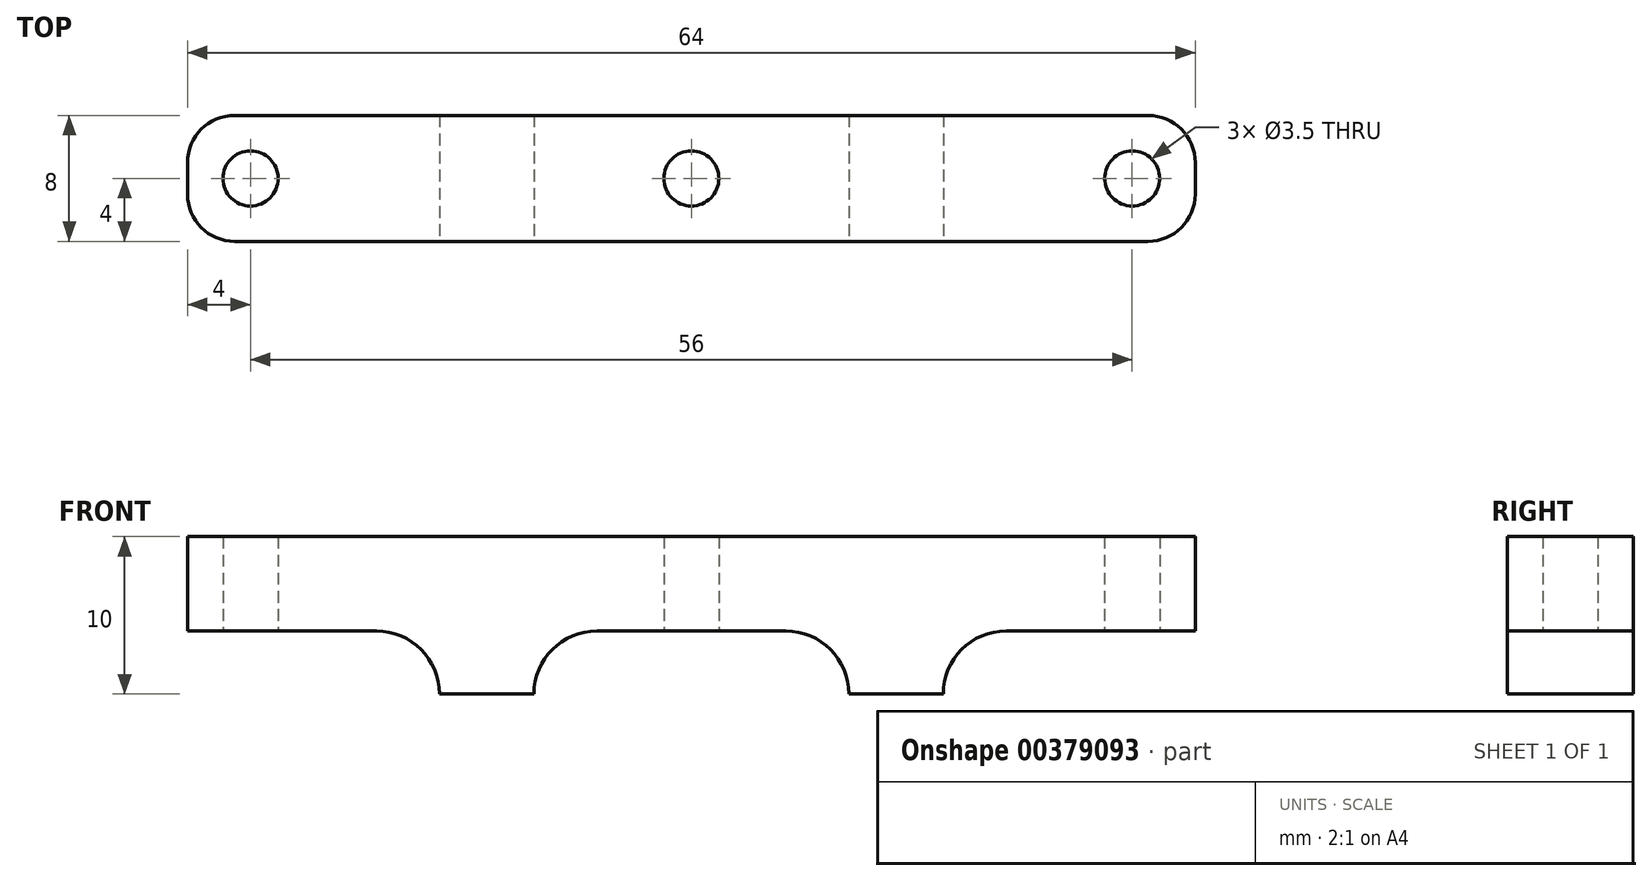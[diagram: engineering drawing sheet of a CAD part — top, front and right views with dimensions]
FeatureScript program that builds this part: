
annotation { "Feature Type Name" : "Feature", "Feature Type Description" : "" }
export const myFeature = defineFeature(function(context is Context, id is Id, definition is map)
    precondition{}
    {
        {
            var Q0;
            Q0=qCreatedBy(makeId("Top.planeOp"),FACE);
            var sketch = newSketch(context, id + "F0", { "sketchPlane" : qUnion([Q0])});
            skLineSegment(sketch, "E0.bottom", {"start": v(0, 0) * mm, "end": v(64, 0) * mm});
            skLineSegment(sketch, "E0.top", {"start": v(0, 8) * mm, "end": v(64, 8) * mm});
            skLineSegment(sketch, "E0.left", {"start": v(0, 0) * mm, "end": v(0, 8) * mm});
            skLineSegment(sketch, "E0.right", {"start": v(64, 0) * mm, "end": v(64, 8) * mm});
            skLineSegment(sketch, "E1", {"start": v(0, 4) * mm, "end": v(64, 4) * mm, "construction": true});
            skCircle(sketch, "E2", {"center": v(4, 4) * mm, "radius": 1.75 * mm});
            skCircle(sketch, "E3", {"center": v(32, 4) * mm, "radius": 1.75 * mm});
            skCircle(sketch, "E4", {"center": v(60, 4) * mm, "radius": 1.75 * mm});
            skSolve(sketch);
        }
        {
            var Q0;
            Q0=makeQuery(id+"F0.imprint","IMPRINT",FACE,{"disambiguationData":[TD([[makeQuery(id+"F0.imprint","IMPRINT",EDGE,{"derivedFrom":sQuery(id+"F0.wireOp",EDGE,"E0.bottom")}),1.0]])]});
            extrude(context, id + "F1", {"entities" : qUnion([Q0]), "depth" : 10 * mm});
        }
        {
            var Q0;
            Q0=makeQuery(id+"F1.opExtrude","SWEPT_FACE",FACE,{"disambiguationData":[OSD([sQuery(id+"F0.wireOp",EDGE,"E0.bottom")])]});
            var sketch = newSketch(context, id + "F2", { "sketchPlane" : qUnion([Q0])});
            skLineSegment(sketch, "E5", {"start": v(0, 4) * mm, "end": v(64, 4) * mm, "construction": true});
            skArc(sketch, "E6", {"start": v(12, 4) * mm, "mid": v(14.83, 2.83) * mm, "end": v(16, 0) * mm});
            skLineSegment(sketch, "E7", {"start": v(16, 0) * mm, "end": v(22, 0) * mm});
            skLineSegment(sketch, "E8", {"start": v(19, 0) * mm, "end": v(19, 4) * mm, "construction": true});
            skArc(sketch, "E9", {"start": v(26, 4) * mm, "mid": v(23.17, 2.83) * mm, "end": v(22, 0) * mm});
            skLineSegment(sketch, "E10", {"start": v(42, 0) * mm, "end": v(48, 0) * mm});
            skLineSegment(sketch, "E11", {"start": v(45, 0) * mm, "end": v(45, 4) * mm, "construction": true});
            skArc(sketch, "E12", {"start": v(38, 4) * mm, "mid": v(40.83, 2.83) * mm, "end": v(42, 0) * mm});
            skArc(sketch, "E13", {"start": v(52, 4) * mm, "mid": v(49.17, 2.83) * mm, "end": v(48, 0) * mm});
            skLineSegment(sketch, "E14", {"start": v(38, 4) * mm, "end": v(26, 4) * mm});
            skLineSegment(sketch, "E15", {"start": v(52, 4) * mm, "end": v(64, 4) * mm});
            skLineSegment(sketch, "E16", {"start": v(64, 4) * mm, "end": v(64, 0) * mm});
            skLineSegment(sketch, "E17", {"start": v(64, 0) * mm, "end": v(48, 0) * mm});
            skLineSegment(sketch, "E18", {"start": v(12, 4) * mm, "end": v(0, 4) * mm});
            skLineSegment(sketch, "E19", {"start": v(0, 4) * mm, "end": v(0, 0) * mm});
            skLineSegment(sketch, "E20", {"start": v(0, 0) * mm, "end": v(16, 0) * mm});
            skLineSegment(sketch, "E21", {"start": v(42, 0) * mm, "end": v(22, 0) * mm});
            skSolve(sketch);
        }
        {
            var Q0;
            Q0 = qSketchRegion(id + "F2", true);
            extrude(context, id + "F3", {"entities" : qUnion([Q0]), "operationType" : NewBodyOperationType.REMOVE, "oppositeDirection" : true, "depth" : 10 * mm});
        }
        {
            var Q0;
            Q0=makeQuery(id+"F1.opExtrude","SWEPT_EDGE",EDGE,{"disambiguationData":[OSD([sQuery(id+"F0.wireOp",EDGE,"E0.bottom"),sQuery(id+"F0.wireOp",EDGE,"E0.left")])]});
            var Q1;
            Q1=makeQuery(id+"F1.opExtrude","SWEPT_EDGE",EDGE,{"disambiguationData":[OSD([sQuery(id+"F0.wireOp",EDGE,"E0.top"),sQuery(id+"F0.wireOp",EDGE,"E0.left")])]});
            var Q2;
            Q2=makeQuery(id+"F1.opExtrude","SWEPT_EDGE",EDGE,{"disambiguationData":[OSD([sQuery(id+"F0.wireOp",EDGE,"E0.bottom"),sQuery(id+"F0.wireOp",EDGE,"E0.right")])]});
            var Q3;
            Q3=makeQuery(id+"F1.opExtrude","SWEPT_EDGE",EDGE,{"disambiguationData":[OSD([sQuery(id+"F0.wireOp",EDGE,"E0.top"),sQuery(id+"F0.wireOp",EDGE,"E0.right")])]});
            fillet(context, id + "F4", {"entities" : qUnion([Q0, Q1, Q2, Q3]), "radius" : 3 * mm, "tangentPropagation" : true, "allowEdgeOverflow" : false});
        }
    });
